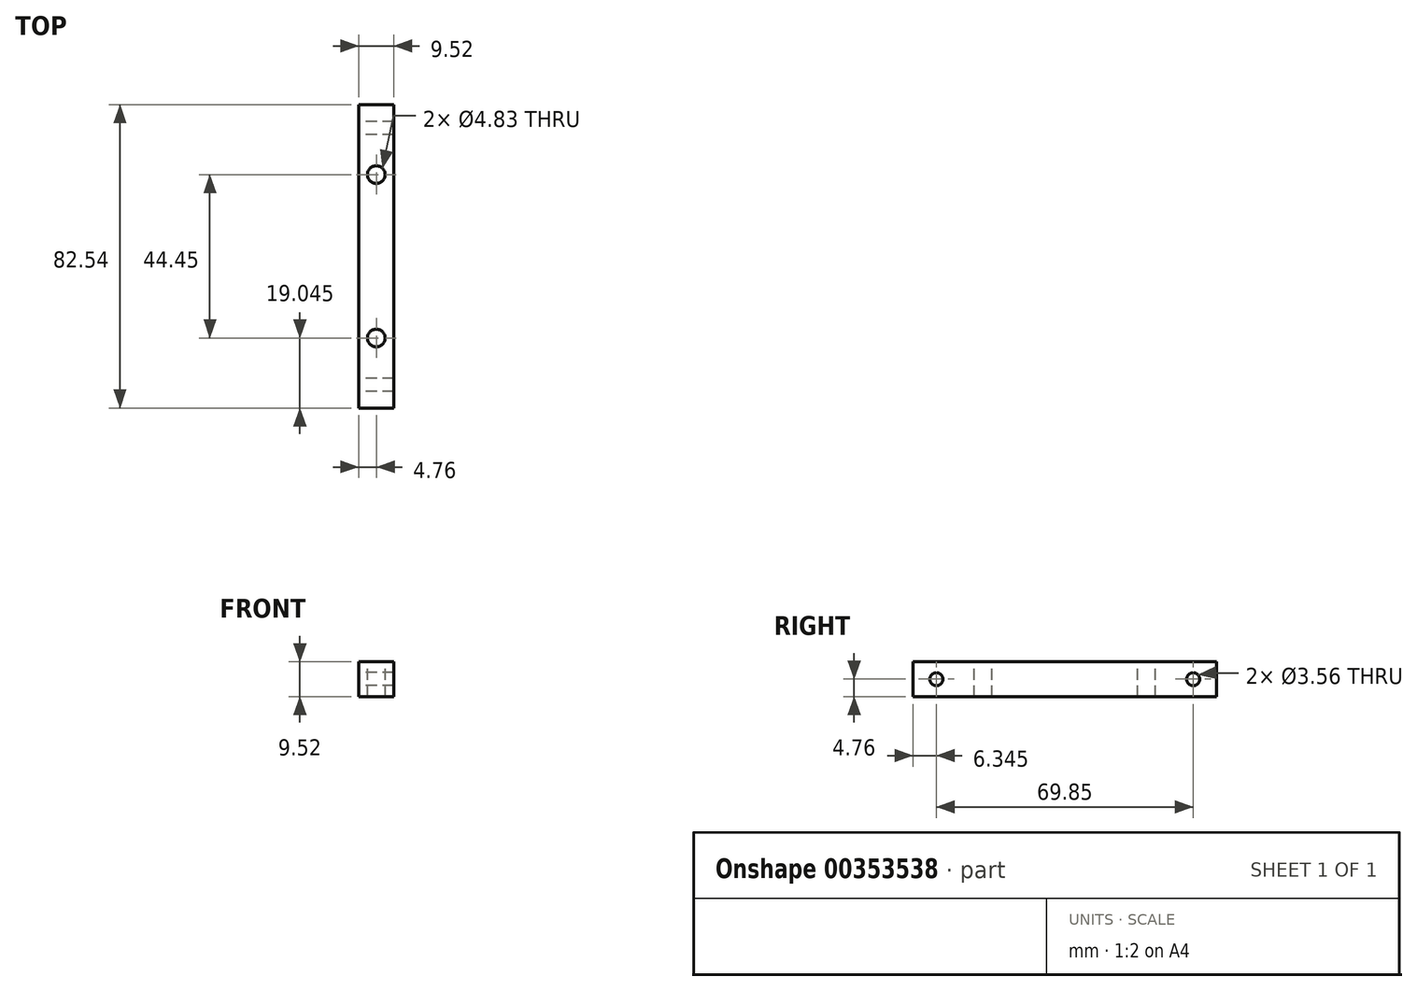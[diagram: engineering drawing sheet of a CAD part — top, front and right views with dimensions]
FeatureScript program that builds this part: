
annotation { "Feature Type Name" : "Feature", "Feature Type Description" : "" }
export const myFeature = defineFeature(function(context is Context, id is Id, definition is map)
    precondition{}
    {
        {
            var Q0;
            Q0=qCreatedBy(makeId("Front.planeOp"),FACE);
            var sketch = newSketch(context, id + "F0", { "sketchPlane" : qUnion([Q0])});
            skLineSegment(sketch, "E0.bottom", {"start": v(4.76, 4.76) * mm, "end": v(-4.76, 4.76) * mm});
            skLineSegment(sketch, "E0.top", {"start": v(4.76, -4.76) * mm, "end": v(-4.76, -4.76) * mm});
            skLineSegment(sketch, "E0.left", {"start": v(4.76, 4.76) * mm, "end": v(4.76, -4.76) * mm});
            skLineSegment(sketch, "E0.right", {"start": v(-4.76, 4.76) * mm, "end": v(-4.76, -4.76) * mm});
            skPoint(sketch, "E0.middle", {"position": v(0, 0) * mm});
            skSolve(sketch);
        }
        {
            var Q0;
            Q0 = qSketchRegion(id + "F0", true);
            extrude(context, id + "F1", {"entities" : qUnion([Q0]), "depth" : 82.55 * mm, "symmetric" : true});
        }
        {
            var Q0;
            Q0=makeQuery(id+"F1.opExtrude","SWEPT_FACE",FACE,{"disambiguationData":[OSD([sQuery(id+"F0.wireOp",EDGE,"E0.right")])]});
            var sketch = newSketch(context, id + "F2", { "sketchPlane" : qUnion([Q0])});
            skCircle(sketch, "E1", {"center": v(-34.93, 0) * mm, "radius": 1.78 * mm});
            skCircle(sketch, "E2", {"center": v(34.93, 0) * mm, "radius": 1.78 * mm});
            skSolve(sketch);
        }
        {
            var Q0;
            Q0=makeQuery(id+"F1.opExtrude","SWEPT_FACE",FACE,{"disambiguationData":[OSD([sQuery(id+"F0.wireOp",EDGE,"E0.bottom")])]});
            var sketch = newSketch(context, id + "F3", { "sketchPlane" : qUnion([Q0])});
            skCircle(sketch, "E3", {"center": v(0, 22.23) * mm, "radius": 2.41 * mm});
            skCircle(sketch, "E4", {"center": v(0, -22.23) * mm, "radius": 2.41 * mm});
            skSolve(sketch);
        }
        {
            var Q0;
            Q0=makeQuery(id+"F3.imprint","IMPRINT",FACE,{"disambiguationData":[TD([[makeQuery(id+"F3.imprint","IMPRINT",EDGE,{"derivedFrom":sQuery(id+"F3.wireOp",EDGE,"E3")}),1.0]])]});
            var Q1;
            Q1=makeQuery(id+"F3.imprint","IMPRINT",FACE,{"disambiguationData":[TD([[makeQuery(id+"F3.imprint","IMPRINT",EDGE,{"derivedFrom":sQuery(id+"F3.wireOp",EDGE,"E4")}),1.0]])]});
            extrude(context, id + "F4", {"entities" : qUnion([Q0, Q1]), "operationType" : NewBodyOperationType.REMOVE, "oppositeDirection" : true, "depth" : 9.52 * mm});
        }
        {
            var Q0;
            Q0=makeQuery(id+"F2.imprint","IMPRINT",FACE,{"disambiguationData":[TD([[makeQuery(id+"F2.imprint","IMPRINT",EDGE,{"derivedFrom":sQuery(id+"F2.wireOp",EDGE,"E2")}),1.0]])]});
            var Q1;
            Q1=makeQuery(id+"F2.imprint","IMPRINT",FACE,{"disambiguationData":[TD([[makeQuery(id+"F2.imprint","IMPRINT",EDGE,{"derivedFrom":sQuery(id+"F2.wireOp",EDGE,"E1")}),1.0]])]});
            extrude(context, id + "F5", {"entities" : qUnion([Q0, Q1]), "operationType" : NewBodyOperationType.REMOVE, "oppositeDirection" : true, "depth" : 9.52 * mm});
        }
    });
